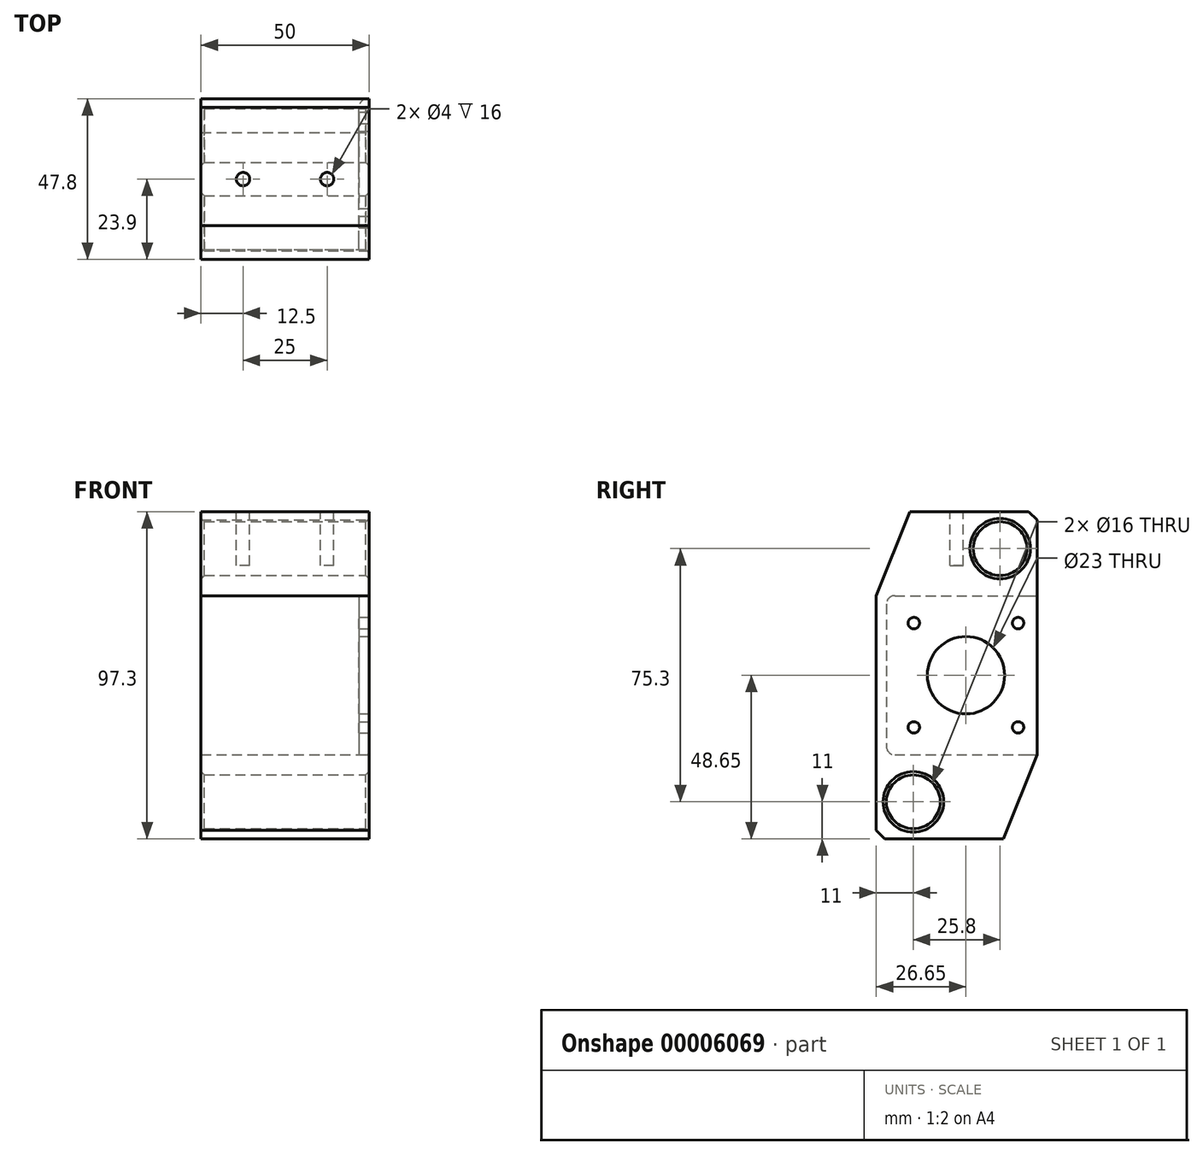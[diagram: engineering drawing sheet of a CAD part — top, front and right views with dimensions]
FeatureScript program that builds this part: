
annotation { "Feature Type Name" : "Feature", "Feature Type Description" : "" }
export const myFeature = defineFeature(function(context is Context, id is Id, definition is map)
    precondition{}
    {
        {
            var Q0;
            Q0=qCreatedBy(makeId("Right.planeOp"),FACE);
            var sketch = newSketch(context, id + "F0", { "sketchPlane" : qUnion([Q0])});
            skLineSegment(sketch, "E0", {"start": v(0, 0) * mm, "end": v(0, 47.3) * mm});
            skLineSegment(sketch, "E1", {"start": v(47.8, 72.3) * mm, "end": v(47.8, 0) * mm});
            skLineSegment(sketch, "E2", {"start": v(0, -25) * mm, "end": v(0, 0) * mm});
            skLineSegment(sketch, "E3", {"start": v(0, -25) * mm, "end": v(47.8, -25) * mm});
            skLineSegment(sketch, "E4", {"start": v(47.8, 72.3) * mm, "end": v(0, 72.3) * mm});
            skLineSegment(sketch, "E5", {"start": v(0, 72.3) * mm, "end": v(0, 47.3) * mm});
            skLineSegment(sketch, "E6", {"start": v(47.8, -25) * mm, "end": v(47.8, 0) * mm});
            skCircle(sketch, "E7", {"center": v(36.8, 61.3) * mm, "radius": 8 * mm});
            skCircle(sketch, "E8", {"center": v(11, -14) * mm, "radius": 8 * mm});
            skLineSegment(sketch, "E9", {"start": v(0, 47.3) * mm, "end": v(47.8, 47.3) * mm});
            skLineSegment(sketch, "E10", {"start": v(0, 0) * mm, "end": v(47.8, 0) * mm});
            skLineSegment(sketch, "E11", {"start": v(3, 47.3) * mm, "end": v(3, 0) * mm});
            skLineSegment(sketch, "E12", {"start": v(5.5, 47.3) * mm, "end": v(5.5, 0) * mm, "construction": true});
            skLineSegment(sketch, "E13", {"start": v(3, 2.5) * mm, "end": v(47.8, 2.5) * mm, "construction": true});
            skLineSegment(sketch, "E14", {"start": v(3, 44.8) * mm, "end": v(47.8, 44.8) * mm, "construction": true});
            skPoint(sketch, "E15", {"position": v(5.5, 44.8) * mm});
            skPoint(sketch, "E16", {"position": v(5.5, 2.5) * mm});
            skLineSegment(sketch, "E17", {"start": v(5.5, 44.8) * mm, "end": v(47.8, 2.5) * mm, "construction": true});
            skLineSegment(sketch, "E18", {"start": v(47.8, 44.8) * mm, "end": v(5.5, 2.5) * mm, "construction": true});
            skLineSegment(sketch, "E19", {"start": v(11.15, 39.15) * mm, "end": v(42.15, 39.15) * mm, "construction": true});
            skLineSegment(sketch, "E20", {"start": v(42.15, 39.15) * mm, "end": v(42.15, 8.15) * mm, "construction": true});
            skLineSegment(sketch, "E21", {"start": v(42.15, 8.15) * mm, "end": v(11.15, 8.15) * mm, "construction": true});
            skLineSegment(sketch, "E22", {"start": v(11.15, 8.15) * mm, "end": v(11.15, 39.15) * mm, "construction": true});
            skCircle(sketch, "E23", {"center": v(11.15, 39.15) * mm, "radius": 1.7 * mm});
            skCircle(sketch, "E24", {"center": v(42.15, 39.15) * mm, "radius": 1.7 * mm});
            skCircle(sketch, "E25", {"center": v(42.15, 8.15) * mm, "radius": 1.7 * mm});
            skCircle(sketch, "E26", {"center": v(11.15, 8.15) * mm, "radius": 1.7 * mm});
            skCircle(sketch, "E27", {"center": v(26.65, 23.65) * mm, "radius": 11.5 * mm});
            skSolve(sketch);
        }
        {
            var Q0;
            {var subQ2=sQuery(id+"F0.wireOp",EDGE,"E0");Q0=makeQuery(id+"F0.imprint","IMPRINT",FACE,{"disambiguationData":[TD([[makeQuery(id+"F0.imprint","IMPRINT",EDGE,{"derivedFrom":subQ2}),-1.0]])]});}
            var Q1;
            {var subQ5=sQuery(id+"F0.wireOp",EDGE,"E4");Q1=makeQuery(id+"F0.imprint","IMPRINT",FACE,{"disambiguationData":[TD([[makeQuery(id+"F0.imprint","IMPRINT",EDGE,{"derivedFrom":subQ5}),1.0]])]});}
            var Q2;
            {var subQ3=sQuery(id+"F0.wireOp",EDGE,"E2");Q2=makeQuery(id+"F0.imprint","IMPRINT",FACE,{"disambiguationData":[TD([[makeQuery(id+"F0.imprint","IMPRINT",EDGE,{"derivedFrom":subQ3}),-1.0]])]});}
            extrude(context, id + "F1", {"entities" : qUnion([Q0, Q1, Q2]), "oppositeDirection" : true, "depth" : 50 * mm});
        }
        {
            var Q0;
            {var subQ0=sQuery(id+"F0.wireOp",EDGE,"E11");Q0=makeQuery(id+"F0.imprint","IMPRINT",FACE,{"disambiguationData":[TD([[makeQuery(id+"F0.imprint","IMPRINT",EDGE,{"derivedFrom":subQ0}),1.0]])]});}
            extrude(context, id + "F2", {"entities" : qUnion([Q0]), "operationType" : NewBodyOperationType.ADD, "oppositeDirection" : true, "depth" : 3 * mm});
        }
        {
            var Q0;
            Q0=makeQuery(id+"F1.opExtrude","SWEPT_EDGE",EDGE,{"disambiguationData":[OSD([sQuery(id+"F0.wireOp",EDGE,"E10"),sQuery(id+"F0.wireOp",EDGE,"E11")])]});
            var Q1;
            Q1=makeQuery(id+"F1.opExtrude","SWEPT_EDGE",EDGE,{"disambiguationData":[OSD([sQuery(id+"F0.wireOp",EDGE,"E9"),sQuery(id+"F0.wireOp",EDGE,"E11")])]});
            var Q2;
            Q2=makeQuery(id+"F2.opExtrude","CAP_EDGE",EDGE,{"disambiguationData":[OSD([sQuery(id+"F0.wireOp",EDGE,"E9")])],"isStart":false});
            var Q3;
            Q3=makeQuery(id+"F2.opExtrude","CAP_EDGE",EDGE,{"disambiguationData":[OSD([sQuery(id+"F0.wireOp",EDGE,"E10")])],"isStart":false});
            var Q4;
            Q4=makeQuery(id+"F2.opExtrude","CAP_EDGE",EDGE,{"disambiguationData":[OSD([sQuery(id+"F0.wireOp",EDGE,"E11")])],"isStart":false});
            var Q5;
            Q5=makeQuery(id+"F2.opExtrude","CAP_EDGE",EDGE,{"disambiguationData":[OSD([sQuery(id+"F0.wireOp",EDGE,"E1")])],"isStart":false});
            fillet(context, id + "F3", {"entities" : qUnion([Q0, Q1, Q2, Q3, Q4, Q5]), "radius" : 2.5 * mm, "tangentPropagation" : true, "allowEdgeOverflow" : false});
        }
        {
            var Q0;
            Q0=makeQuery(id+"F1.opExtrude","CAP_EDGE",EDGE,{"disambiguationData":[OSD([sQuery(id+"F0.wireOp",EDGE,"E7")])],"isStart":true});
            var Q1;
            Q1=makeQuery(id+"F1.opExtrude","CAP_EDGE",EDGE,{"disambiguationData":[OSD([sQuery(id+"F0.wireOp",EDGE,"E8")])],"isStart":true});
            var Q2;
            Q2=makeQuery(id+"F1.opExtrude","CAP_EDGE",EDGE,{"disambiguationData":[OSD([sQuery(id+"F0.wireOp",EDGE,"E8")])],"isStart":false});
            var Q3;
            Q3=makeQuery(id+"F1.opExtrude","CAP_EDGE",EDGE,{"disambiguationData":[OSD([sQuery(id+"F0.wireOp",EDGE,"E7")])],"isStart":false});
            chamfer(context, id + "F4", {"entities" : qUnion([Q0, Q1, Q2, Q3]), "width" : 1 * mm, "tangentPropagation" : true});
        }
        {
            var Q0;
            Q0=makeQuery(id+"F1.opExtrude","SWEPT_FACE",FACE,{"disambiguationData":[OSD([sQuery(id+"F0.wireOp",EDGE,"E4")])]});
            var sketch = newSketch(context, id + "F5", { "sketchPlane" : qUnion([Q0])});
            skLineSegment(sketch, "E28", {"start": v(-25, 47.8) * mm, "end": v(-25, 23.9) * mm, "construction": true});
            skLineSegment(sketch, "E29", {"start": v(-25, 23.9) * mm, "end": v(-12.5, 23.9) * mm, "construction": true});
            skLineSegment(sketch, "E30", {"start": v(-25, 23.9) * mm, "end": v(-37.5, 23.9) * mm, "construction": true});
            skCircle(sketch, "E31", {"center": v(-12.5, 23.9) * mm, "radius": 2 * mm});
            skCircle(sketch, "E32", {"center": v(-37.5, 23.9) * mm, "radius": 2 * mm});
            skSolve(sketch);
        }
        {
            var Q0;
            Q0 = qSketchRegion(id + "F5", true);
            extrude(context, id + "F6", {"entities" : qUnion([Q0]), "operationType" : NewBodyOperationType.REMOVE, "oppositeDirection" : true, "depth" : 16 * mm});
        }
        {
            var Q0;
            Q0=makeQuery(id+"F1.opExtrude","SWEPT_EDGE",EDGE,{"disambiguationData":[OSD([sQuery(id+"F0.wireOp",EDGE,"E1"),sQuery(id+"F0.wireOp",EDGE,"E4")])]});
            var Q1;
            Q1=makeQuery(id+"F1.opExtrude","SWEPT_EDGE",EDGE,{"disambiguationData":[OSD([sQuery(id+"F0.wireOp",EDGE,"E2"),sQuery(id+"F0.wireOp",EDGE,"E3")])]});
            chamfer(context, id + "F7", {"entities" : qUnion([Q0, Q1]), "width" : 2.5 * mm, "tangentPropagation" : true});
        }
        {
            var Q0;
            Q0=makeQuery(id+"F1.opExtrude","SWEPT_EDGE",EDGE,{"disambiguationData":[OSD([sQuery(id+"F0.wireOp",EDGE,"E4"),sQuery(id+"F0.wireOp",EDGE,"E5")])]});
            var Q1;
            Q1=makeQuery(id+"F1.opExtrude","SWEPT_EDGE",EDGE,{"disambiguationData":[OSD([sQuery(id+"F0.wireOp",EDGE,"E3"),sQuery(id+"F0.wireOp",EDGE,"E6")])]});
            chamfer(context, id + "F8", {"entities" : qUnion([Q0, Q1]), "chamferType" : ChamferType.TWO_OFFSETS, "width1" : 10 * mm, "oppositeDirection" : false, "width2" : 25 * mm, "tangentPropagation" : true});
        }
    });
